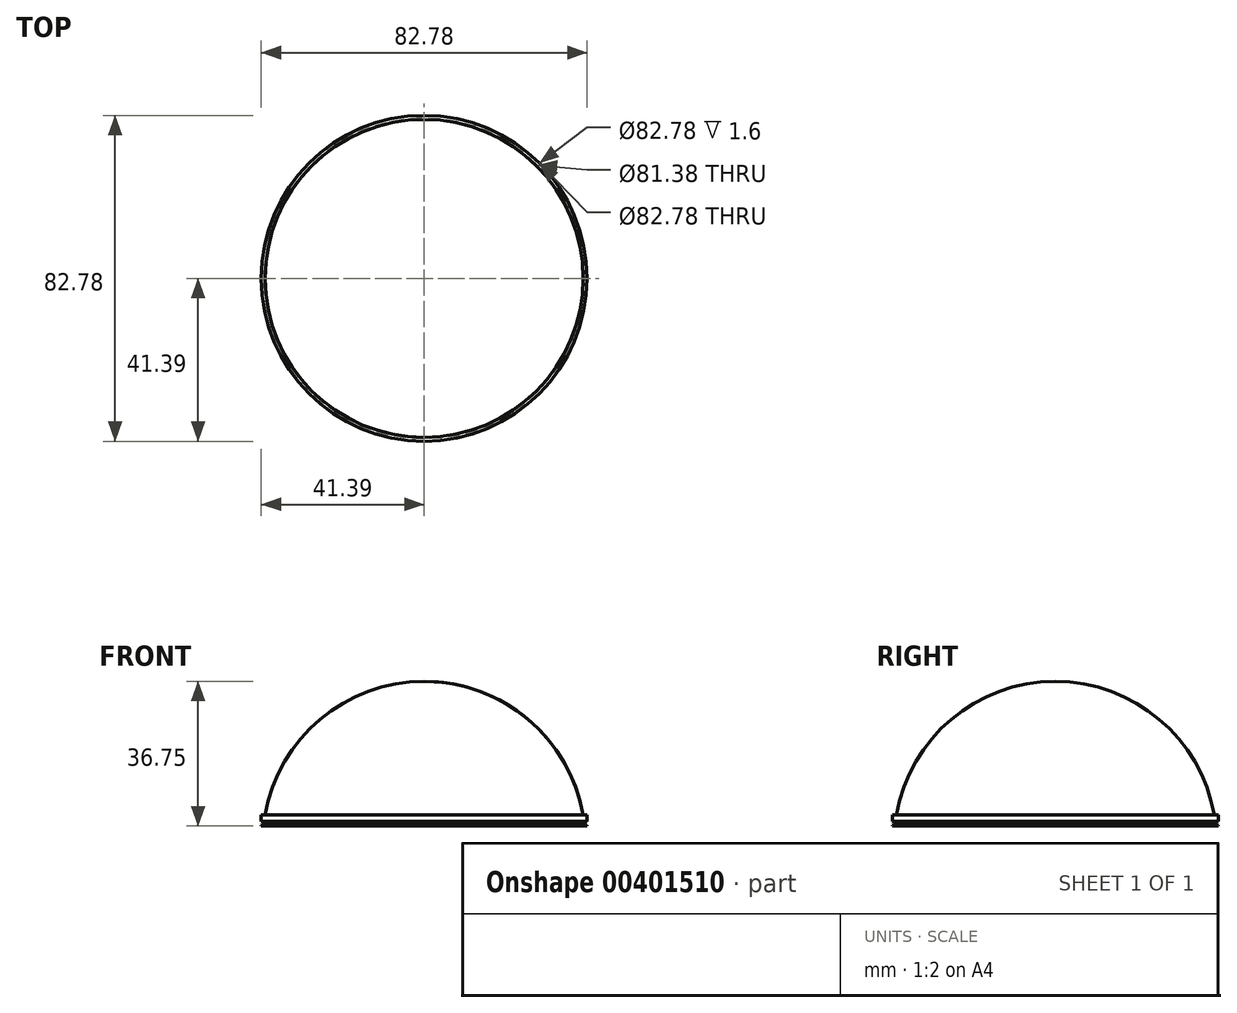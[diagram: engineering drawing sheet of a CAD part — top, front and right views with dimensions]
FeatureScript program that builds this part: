
annotation { "Feature Type Name" : "Feature", "Feature Type Description" : "" }
export const myFeature = defineFeature(function(context is Context, id is Id, definition is map)
    precondition{}
    {
        {
            var Q0;
            Q0=qCreatedBy(makeId("Front.planeOp"),FACE);
            var sketch = newSketch(context, id + "F0", { "sketchPlane" : qUnion([Q0])});
            skArc(sketch, "E0", {"start": v(40.39, 2.8) * mm, "mid": v(26.38, 27.14) * mm, "end": v(0, 36.75) * mm});
            skLineSegment(sketch, "E1", {"start": v(-40.78, 0) * mm, "end": v(40.78, 0) * mm, "construction": true});
            skLineSegment(sketch, "E2", {"start": v(15.73, 2.8) * mm, "end": v(51.43, 2.8) * mm, "construction": true});
            skLineSegment(sketch, "E3", {"start": v(41.39, 2.8) * mm, "end": v(41.39, 1.2) * mm});
            skLineSegment(sketch, "E4", {"start": v(40.39, 2.8) * mm, "end": v(41.39, 2.8) * mm});
            skLineSegment(sketch, "E5", {"start": v(41.39, 1.2) * mm, "end": v(40.69, 1) * mm});
            skLineSegment(sketch, "E6", {"start": v(40.69, 1) * mm, "end": v(40.69, 0.4) * mm});
            skLineSegment(sketch, "E7", {"start": v(40.69, 0.4) * mm, "end": v(41.39, 0.2) * mm});
            skLineSegment(sketch, "E8", {"start": v(0, 0) * mm, "end": v(0, 50.04) * mm, "construction": true});
            skLineSegment(sketch, "E9.trimOffspring", {"start": v(41.39, 0.2) * mm, "end": v(41.39, 0) * mm});
            skSolve(sketch);
        }
        {
            var Q0;
            Q0=qSketchRegion(id+"F0",true);
            var Q1;
            Q1=sQuery(id+"F0.wireOp",EDGE,"E0");
            var Q2;
            Q2=sQuery(id+"F0.wireOp",EDGE,"E4");
            var Q3;
            Q3=sQuery(id+"F0.wireOp",EDGE,"E3");
            var Q4;
            Q4=sQuery(id+"F0.wireOp",EDGE,"E5");
            var Q5;
            Q5=sQuery(id+"F0.wireOp",EDGE,"E6");
            var Q6;
            Q6=sQuery(id+"F0.wireOp",EDGE,"E7");
            var Q7;
            Q7=sQuery(id+"F0.wireOp",EDGE,"E9.trimOffspring");
            var Q8;
            Q8=sQuery(id+"F0.wireOp",EDGE,"E8");
            revolve(context, id + "F1", {"bodyType" : ToolBodyType.SURFACE, "entities" : qUnion([Q0]), "surfaceEntities" : qUnion([Q1, Q2, Q3, Q4, Q5, Q6, Q7]), "axis" : qUnion([Q8]), "revolveType" : RevolveType.FULL});
        }
    });
